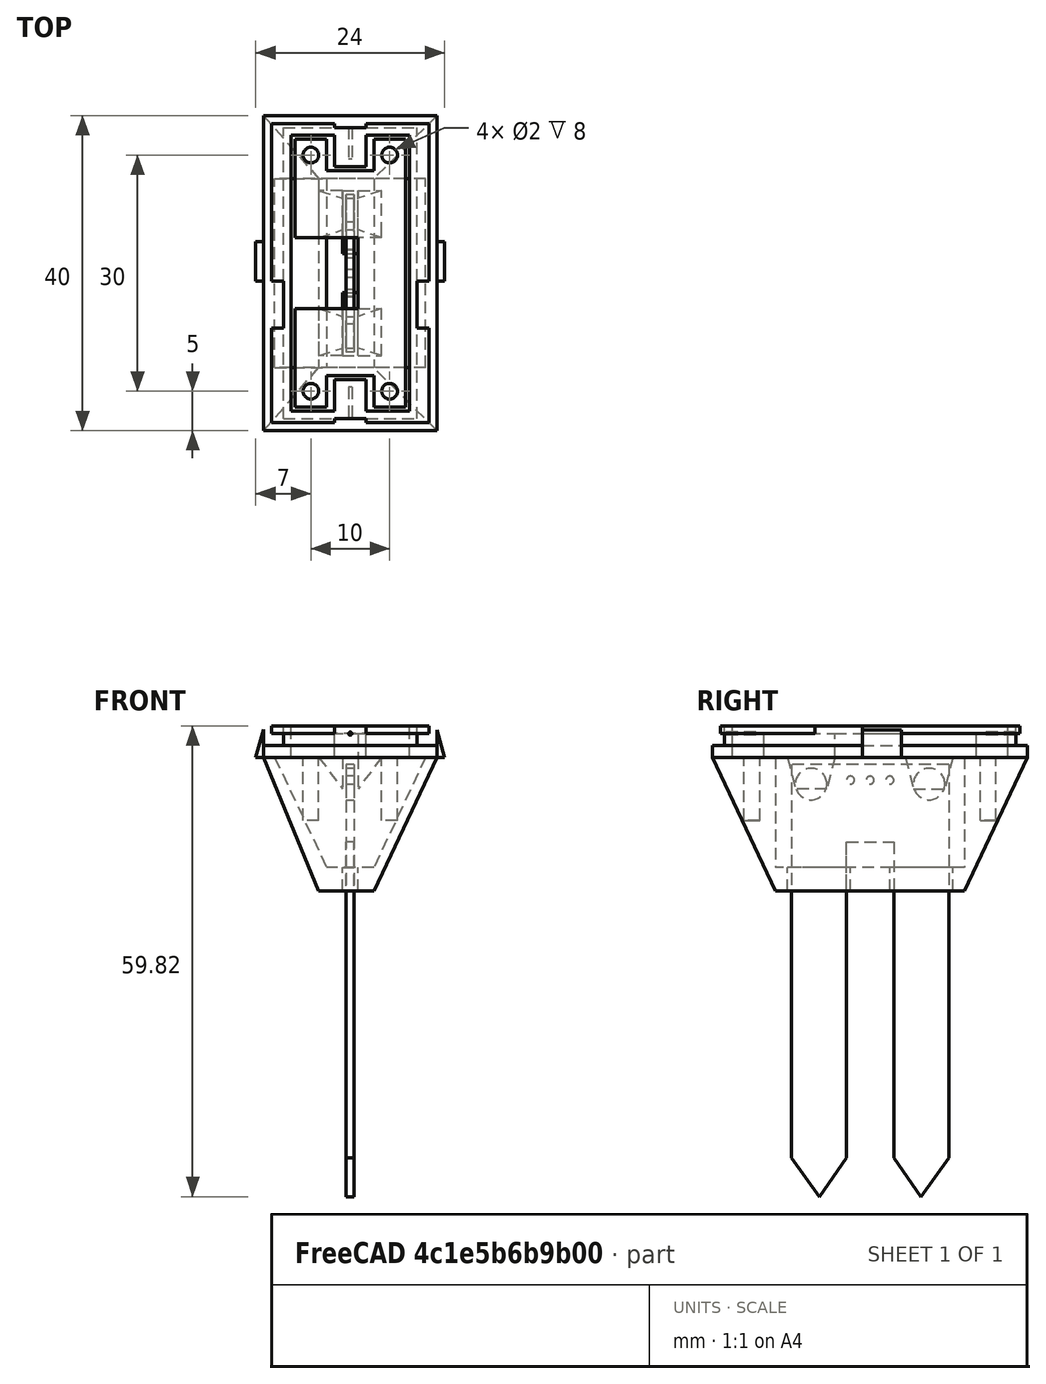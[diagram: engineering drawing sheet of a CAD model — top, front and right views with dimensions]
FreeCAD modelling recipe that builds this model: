
FCSTD DOCUMENT  (FreeCAD 0.17R13522 (Git))
Label: moisture_sensor
License: All rights reserved
LicenseURL: http://en.wikipedia.org/wiki/All_rights_reserved
objects: Part::Box×9, Part::Cylinder×8, Part::MultiFuse×7, Part::Wedge×6, Part::Cut×4, Part::FeaturePython×2
note: 36 computed .brp shape members not serialized (recipe doc carries the construction recipe); baked Part::Feature solids carry a one-line shape summary decoded from their .brp

FEATURE [Part::FeaturePython] BaseSensorMount_01  # a2plus imported part (geometry in sourceFile) (typed FeaturePython)
  fixedPosition = true
  sourceFile = <userpath>/PycharmProjects/PlantMonitor/Assembly/BaseParts/BaseSensorMount.FCStd
  timeLastImport = 1.52832e+09
  updateColors = true
FEATURE [Part::FeaturePython] MoistureSensor_01  # a2plus imported part (geometry in sourceFile) (typed FeaturePython)
  Placement = pos=(11.5,20,-36) rot=(0,-1,0;1.5708rad)
  fixedPosition = false
  sourceFile = <userpath>/PycharmProjects/PlantMonitor/Assembly/ElectronicShapes/MoistureSensor.FCStd
  timeLastImport = 1.53117e+09
  updateColors = true
FEATURE [Part::Wedge] Wedge
  AttacherType = Attacher::AttachEngine3D
  Placement = pos=(-10,40,0) rot=(0,0.707107,-0.707107;3.14159rad)
  X2max = 15
  X2min = 8
  Xmax = 22
  Xmin = 0
  Ymax = 17
  Ymin = 0
  Z2max = 32
  Z2min = 8
  Zmax = 40
  Zmin = 0
FEATURE [Part::Wedge] Wedge001  label="CuttuingWedge"
  AttacherType = Attacher::AttachEngine3D
  Placement = pos=(-10,40,3) rot=(0,0.707107,-0.707107;3.14159rad)
  X2max = 14
  X2min = 8
  Xmax = 22
  Xmin = 0
  Ymax = 17
  Ymin = 0
  Z2max = 32
  Z2min = 8
  Zmax = 32
  Zmin = 8
FEATURE [Part::Cut] Cut
  Base = -> Wedge
  Placement = pos=(32,0,0) rot=(0,0,1;0rad)
  Tool = -> Wedge001
FEATURE [Part::Box] Box  label="spacefilling"
  AttacherType = Attacher::AttachEngine3D
  Height = 1.5
  Length = 4
  Placement = pos=(9,2.5,0) rot=(0,0,1;0rad)
  Width = 4
FEATURE [Part::Box] Box001  label="spacefilling001"
  AttacherType = Attacher::AttachEngine3D
  Height = 1.5
  Length = 4
  Placement = pos=(9,33.5,0) rot=(0,0,1;0rad)
  Width = 4
FEATURE [Part::MultiFuse] Fusion  label="SensormountOutershell"
  Shapes = -> [Box001,Box,Cut,BaseSensorMount_01]
FEATURE [Part::Box] Box002  label="forkhole1"
  AttacherType = Attacher::AttachEngine3D
  Height = 5
  Length = 2
  Placement = pos=(10,9.5,-17) rot=(0,0,1;0rad)
  Width = 8
FEATURE [Part::Box] Box003  label="forkhole2"
  AttacherType = Attacher::AttachEngine3D
  Height = 5
  Length = 2
  Placement = pos=(10,22.5,-17) rot=(0,0,1;0rad)
  Width = 8
FEATURE [Part::Cylinder] Cylinder  label="screwhole1"
  Angle = 360
  AttacherType = Attacher::AttachEngine3D
  Height = 8
  Placement = pos=(6,5,-8) rot=(0,0,1;0rad)
  Radius = 1
FEATURE [Part::Cylinder] Cylinder001  label="screwhole002"
  Angle = 360
  AttacherType = Attacher::AttachEngine3D
  Height = 8
  Placement = pos=(6,35,-8) rot=(0,0,1;0rad)
  Radius = 1
FEATURE [Part::Cylinder] Cylinder002  label="screwhole003"
  Angle = 360
  AttacherType = Attacher::AttachEngine3D
  Height = 8
  Placement = pos=(16,5,-8) rot=(0,0,1;0rad)
  Radius = 1
FEATURE [Part::Cylinder] Cylinder003  label="screwhole004"
  Angle = 360
  AttacherType = Attacher::AttachEngine3D
  Height = 8
  Placement = pos=(16,35,-8) rot=(0,0,1;0rad)
  Radius = 1
FEATURE [Part::MultiFuse] Fusion001  label="holes and cuts"
  Shapes = -> [Box002,Cylinder001,Cylinder002,Cylinder003,Box003,Cylinder]
FEATURE [Part::Cut] Cut001  label="MountWithCutsAndHoles"
  Base = -> Fusion
  Tool = -> Fusion001
FEATURE [Part::Box] Box004  label="upperplate"
  AttacherType = Attacher::AttachEngine3D
  Height = 3
  Length = 14
  Placement = pos=(4,3,0) rot=(0,0,1;0rad)
  Width = 12.5
FEATURE [Part::Box] Box005  label="mounthole"
  AttacherType = Attacher::AttachEngine3D
  Height = 5
  Length = 6
  Placement = pos=(8,3,0) rot=(0,0,1;0rad)
  Width = 4
FEATURE [Part::Cylinder] Cylinder004  label="screwhole"
  Angle = 360
  AttacherType = Attacher::AttachEngine3D
  Height = 6
  Placement = pos=(6,5,-2) rot=(0,0,1;0rad)
  Radius = 1
FEATURE [Part::Cylinder] Cylinder005  label="screwhole005"
  Angle = 360
  AttacherType = Attacher::AttachEngine3D
  Height = 6
  Placement = pos=(16,5,-2) rot=(0,0,1;0rad)
  Radius = 1
FEATURE [Part::MultiFuse] Fusion002
  Shapes = -> [Box005,Cylinder005,Cylinder004]
FEATURE [Part::Cut] Cut002
  Base = -> Box004
  Tool = -> Fusion002
FEATURE [Part::Wedge] Wedge002  label="triange"
  AttacherType = Attacher::AttachEngine3D
  Placement = pos=(12,10.5,0) rot=(-1,0,0;1.5708rad)
  X2max = 0
  X2min = 0
  Xmax = 3
  Xmin = 0
  Ymax = 4
  Ymin = 0
  Z2max = 4
  Z2min = 0
  Zmax = 5
  Zmin = -1
FEATURE [Part::Wedge] Wedge003  label="triange001"
  AttacherType = Attacher::AttachEngine3D
  Placement = pos=(10,14.5,0) rot=(0,0.707107,-0.707107;3.14159rad)
  X2max = 0
  X2min = 0
  Xmax = 3
  Xmin = 0
  Ymax = 4
  Ymin = 0
  Z2max = 4
  Z2min = 0
  Zmax = 5
  Zmin = -1
FEATURE [Part::MultiFuse] Fusion003  label="sensorholder"
  Shapes = -> [Cut002,Wedge002,Wedge003]
FEATURE [Part::Box] Box006  label="mounthole001"
  AttacherType = Attacher::AttachEngine3D
  Height = 5
  Length = 6
  Placement = pos=(8,3,0) rot=(0,0,1;0rad)
  Width = 4
FEATURE [Part::Box] Box007  label="upperplate001"
  AttacherType = Attacher::AttachEngine3D
  Height = 3
  Length = 14
  Placement = pos=(4,3,0) rot=(0,0,1;0rad)
  Width = 12.5
FEATURE [Part::Cylinder] Cylinder006  label="screwhole006"
  Angle = 360
  AttacherType = Attacher::AttachEngine3D
  Height = 6
  Placement = pos=(16,5,-2) rot=(0,0,1;0rad)
  Radius = 1
FEATURE [Part::Cylinder] Cylinder007  label="screwhole007"
  Angle = 360
  AttacherType = Attacher::AttachEngine3D
  Height = 6
  Placement = pos=(6,5,-2) rot=(0,0,1;0rad)
  Radius = 1
FEATURE [Part::MultiFuse] Fusion004
  Shapes = -> [Box006,Cylinder006,Cylinder007]
FEATURE [Part::Cut] Cut003
  Base = -> Box007
  Tool = -> Fusion004
FEATURE [Part::Wedge] Wedge004  label="triange002"
  AttacherType = Attacher::AttachEngine3D
  Placement = pos=(12,10.5,0) rot=(-1,0,0;1.5708rad)
  X2max = 0
  X2min = 0
  Xmax = 3
  Xmin = 0
  Ymax = 4
  Ymin = 0
  Z2max = 4
  Z2min = 0
  Zmax = 5
  Zmin = -1
FEATURE [Part::Wedge] Wedge005  label="triange003"
  AttacherType = Attacher::AttachEngine3D
  Placement = pos=(10,14.5,0) rot=(0,0.707107,-0.707107;3.14159rad)
  X2max = 0
  X2min = 0
  Xmax = 3
  Xmin = 0
  Ymax = 4
  Ymin = 0
  Z2max = 4
  Z2min = 0
  Zmax = 5
  Zmin = -1
FEATURE [Part::MultiFuse] Fusion005  label="sensorholder001"
  Placement = pos=(22,40,0) rot=(0,0,1;3.14159rad)
  Shapes = -> [Cut003,Wedge004,Wedge005]
FEATURE [Part::Box] Box008  label="concatcube"
  AttacherType = Attacher::AttachEngine3D
  Height = 3
  Length = 6
  Placement = pos=(12,15,0) rot=(0,0,1;0rad)
  Width = 10
FEATURE [Part::MultiFuse] Fusion006  label="CompleteSensorHolder"
  Shapes = -> [Fusion003,Fusion005,Box008]
